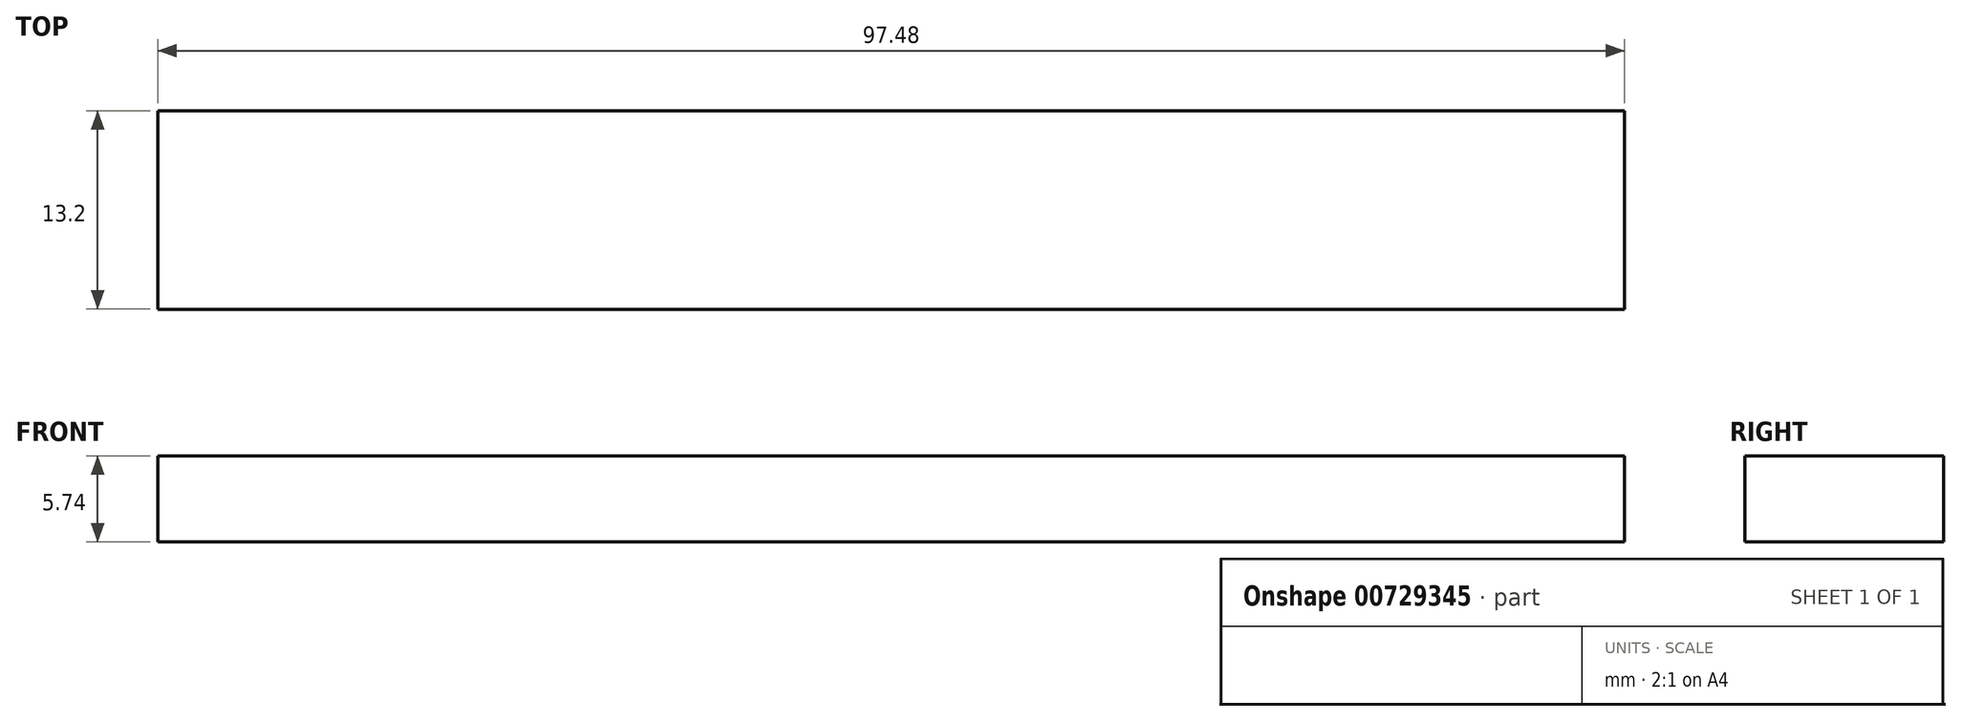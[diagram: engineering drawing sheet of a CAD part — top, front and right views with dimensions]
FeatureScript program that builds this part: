
annotation { "Feature Type Name" : "Feature", "Feature Type Description" : "" }
export const myFeature = defineFeature(function(context is Context, id is Id, definition is map)
    precondition{}
    {
        {
            var Q0;
            Q0=qCreatedBy(makeId("Front.planeOp"),FACE);
            var sketch = newSketch(context, id + "F0", { "sketchPlane" : qUnion([Q0])});
            skLineSegment(sketch, "E0.bottom", {"start": v(-48.74, -2.87) * mm, "end": v(48.74, -2.87) * mm});
            skLineSegment(sketch, "E0.top", {"start": v(-48.74, 2.87) * mm, "end": v(48.74, 2.87) * mm});
            skLineSegment(sketch, "E0.left", {"start": v(-48.74, -2.87) * mm, "end": v(-48.74, 2.87) * mm});
            skLineSegment(sketch, "E0.right", {"start": v(48.74, -2.87) * mm, "end": v(48.74, 2.87) * mm});
            skPoint(sketch, "E0.middle", {"position": v(0, 0) * mm});
            skSolve(sketch);
        }
        {
            var Q0;
            Q0=makeQuery(id+"F0.imprint","IMPRINT",FACE,{"disambiguationData":[TD([[makeQuery(id+"F0.imprint","IMPRINT",EDGE,{"derivedFrom":sQuery(id+"F0.wireOp",EDGE,"E0.bottom")}),1.0]])]});
            extrude(context, id + "F1", {"entities" : qUnion([Q0]), "endBound" : BoundingType.SYMMETRIC, "oppositeDirection" : true, "depth" : 13.2 * mm, "offsetDistance" : 25.4 * mm});
        }
    });
